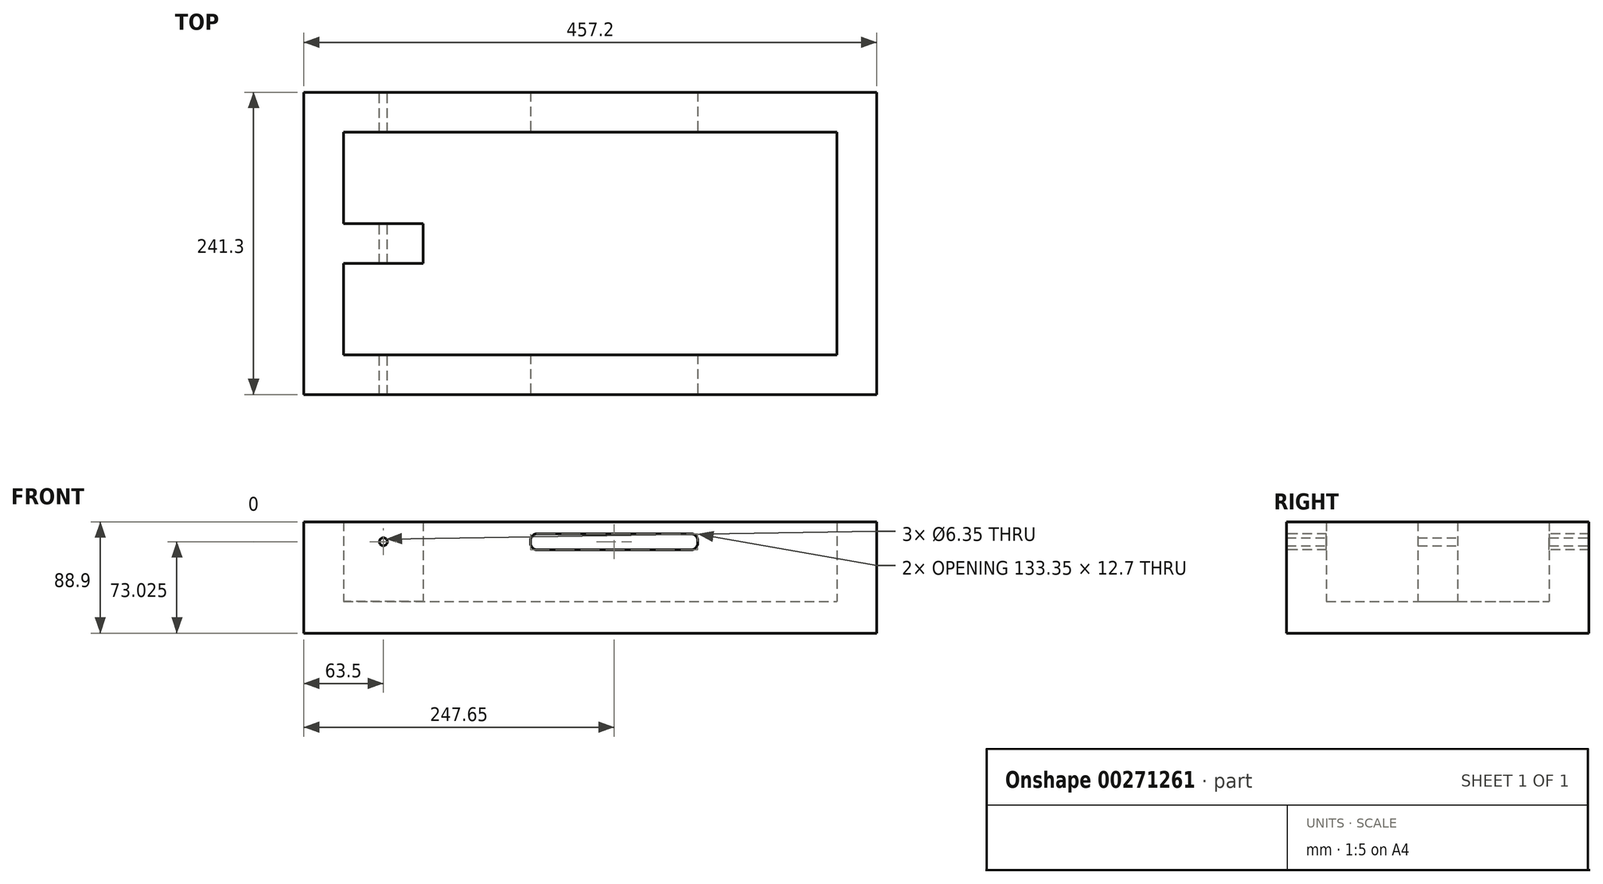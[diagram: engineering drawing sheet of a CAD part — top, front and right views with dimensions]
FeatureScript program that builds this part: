
annotation { "Feature Type Name" : "Feature", "Feature Type Description" : "" }
export const myFeature = defineFeature(function(context is Context, id is Id, definition is map)
    precondition{}
    {
        {
            var Q0;
            Q0=qCreatedBy(makeId("Front.planeOp"),FACE);
            var sketch = newSketch(context, id + "F0", { "sketchPlane" : qUnion([Q0])});
            skLineSegment(sketch, "E0.bottom", {"start": v(0, 0) * mm, "end": v(457.2, 0) * mm});
            skLineSegment(sketch, "E0.top", {"start": v(0, 63.5) * mm, "end": v(457.2, 63.5) * mm});
            skLineSegment(sketch, "E0.left", {"start": v(0, 0) * mm, "end": v(0, 63.5) * mm});
            skLineSegment(sketch, "E0.right", {"start": v(457.2, 0) * mm, "end": v(457.2, 63.5) * mm});
            skSolve(sketch);
        }
        {
            var Q0;
            Q0=makeQuery(id+"F0.imprint","IMPRINT",FACE,{"disambiguationData":[TD([[makeQuery(id+"F0.imprint","IMPRINT",EDGE,{"derivedFrom":sQuery(id+"F0.wireOp",EDGE,"E0.bottom")}),1.0]])]});
            extrude(context, id + "F1", {"entities" : qUnion([Q0]), "depth" : 31.75 * mm});
        }
        {
            var Q0;
            Q0=makeQuery(id+"F1.opExtrude","CAP_FACE",FACE,{"disambiguationData":[OSD([sQuery(id+"F0.wireOp",EDGE,"E0.bottom"),sQuery(id+"F0.wireOp",EDGE,"E0.top"),sQuery(id+"F0.wireOp",EDGE,"E0.left"),sQuery(id+"F0.wireOp",EDGE,"E0.right")])],"isStart":false});
            var sketch = newSketch(context, id + "F2", { "sketchPlane" : qUnion([Q0])});
            skLineSegment(sketch, "E1.bottom", {"start": v(457.2, 63.5) * mm, "end": v(425.45, 63.5) * mm});
            skLineSegment(sketch, "E1.top", {"start": v(457.2, 0) * mm, "end": v(425.45, 0) * mm});
            skLineSegment(sketch, "E1.left", {"start": v(457.2, 63.5) * mm, "end": v(457.2, 0) * mm});
            skLineSegment(sketch, "E1.right", {"start": v(425.45, 63.5) * mm, "end": v(425.45, 0) * mm});
            skSolve(sketch);
        }
        {
            var Q0;
            Q0=makeQuery(id+"F2.imprint","IMPRINT",FACE,{"disambiguationData":[TD([[makeQuery(id+"F2.imprint","IMPRINT",EDGE,{"derivedFrom":sQuery(id+"F2.wireOp",EDGE,"E1.bottom")}),-1.0]])]});
            extrude(context, id + "F3", {"entities" : qUnion([Q0]), "operationType" : NewBodyOperationType.ADD, "depth" : 177.8 * mm});
        }
        {
            var Q0;
            Q0=makeQuery(id+"F3.opExtrude","CAP_FACE",FACE,{"disambiguationData":[OSD([sQuery(id+"F2.wireOp",EDGE,"E1.bottom"),sQuery(id+"F2.wireOp",EDGE,"E1.top"),sQuery(id+"F2.wireOp",EDGE,"E1.left"),sQuery(id+"F2.wireOp",EDGE,"E1.right")])],"isStart":false});
            var sketch = newSketch(context, id + "F4", { "sketchPlane" : qUnion([Q0])});
            skLineSegment(sketch, "E2.bottom", {"start": v(457.2, 0) * mm, "end": v(0, 0) * mm});
            skLineSegment(sketch, "E2.top", {"start": v(457.2, 63.5) * mm, "end": v(0, 63.5) * mm});
            skLineSegment(sketch, "E2.left", {"start": v(457.2, 0) * mm, "end": v(457.2, 63.5) * mm});
            skLineSegment(sketch, "E2.right", {"start": v(0, 0) * mm, "end": v(0, 63.5) * mm});
            skSolve(sketch);
        }
        {
            var Q0;
            {var subQ0=sQuery(id+"F4.wireOp",EDGE,"E2.left");Q0=makeQuery(id+"F4.imprint","IMPRINT",FACE,{"disambiguationData":[TD([[makeQuery(id+"F4.imprint","IMPRINT",EDGE,{"derivedFrom":subQ0}),1.0]])]});}
            var Q1;
            {var subQ2=sQuery(id+"F4.wireOp",EDGE,"E2.right");Q1=makeQuery(id+"F4.imprint","IMPRINT",FACE,{"disambiguationData":[TD([[makeQuery(id+"F4.imprint","IMPRINT",EDGE,{"derivedFrom":subQ2}),-1.0]])]});}
            extrude(context, id + "F5", {"entities" : qUnion([Q0, Q1]), "operationType" : NewBodyOperationType.ADD, "depth" : 31.75 * mm});
        }
        {
            var Q0;
            Q0=makeQuery(id+"F1.opExtrude","CAP_FACE",FACE,{"disambiguationData":[OSD([sQuery(id+"F0.wireOp",EDGE,"E0.bottom"),sQuery(id+"F0.wireOp",EDGE,"E0.top"),sQuery(id+"F0.wireOp",EDGE,"E0.left"),sQuery(id+"F0.wireOp",EDGE,"E0.right")])],"isStart":false});
            var sketch = newSketch(context, id + "F6", { "sketchPlane" : qUnion([Q0])});
            skLineSegment(sketch, "E3.bottom", {"start": v(0, 63.5) * mm, "end": v(31.75, 63.5) * mm});
            skLineSegment(sketch, "E3.top", {"start": v(0, 0) * mm, "end": v(31.75, 0) * mm});
            skLineSegment(sketch, "E3.left", {"start": v(0, 63.5) * mm, "end": v(0, 0) * mm});
            skLineSegment(sketch, "E3.right", {"start": v(31.75, 63.5) * mm, "end": v(31.75, 0) * mm});
            skSolve(sketch);
        }
        {
            var Q0;
            Q0=makeQuery(id+"F6.imprint","IMPRINT",FACE,{"disambiguationData":[TD([[makeQuery(id+"F6.imprint","IMPRINT",EDGE,{"derivedFrom":sQuery(id+"F6.wireOp",EDGE,"E3.bottom")}),-1.0]])]});
            extrude(context, id + "F7", {"entities" : qUnion([Q0]), "operationType" : NewBodyOperationType.ADD, "depth" : 177.8 * mm});
        }
        {
            var Q0;
            Q0=makeQuery(id+"F7.opExtrude","SWEPT_FACE",FACE,{"disambiguationData":[OSD([sQuery(id+"F6.wireOp",EDGE,"E3.right")])]});
            var sketch = newSketch(context, id + "F8", { "sketchPlane" : qUnion([Q0])});
            skLineSegment(sketch, "E4", {"start": v(-209.55, 63.5) * mm, "end": v(-120.65, 63.5) * mm});
            skLineSegment(sketch, "E5", {"start": v(-120.65, 63.5) * mm, "end": v(-120.65, 0) * mm});
            skLineSegment(sketch, "E6.bottom", {"start": v(-136.53, 63.5) * mm, "end": v(-104.78, 63.5) * mm});
            skLineSegment(sketch, "E6.top", {"start": v(-136.53, 0) * mm, "end": v(-104.78, 0) * mm});
            skLineSegment(sketch, "E6.left", {"start": v(-136.53, 63.5) * mm, "end": v(-136.53, 0) * mm});
            skLineSegment(sketch, "E6.right", {"start": v(-104.78, 63.5) * mm, "end": v(-104.78, 0) * mm});
            skPoint(sketch, "E6.middle", {"position": v(-120.65, 31.75) * mm});
            skSolve(sketch);
        }
        {
            var Q0;
            {var subQ0=sQuery(id+"F8.wireOp",EDGE,"E5");Q0=makeQuery(id+"F8.imprint","IMPRINT",FACE,{"disambiguationData":[TD([[makeQuery(id+"F8.imprint","IMPRINT",EDGE,{"derivedFrom":subQ0}),-1.0]])]});}
            var Q1;
            {var subQ0=sQuery(id+"F8.wireOp",EDGE,"E5");Q1=makeQuery(id+"F8.imprint","IMPRINT",FACE,{"disambiguationData":[TD([[makeQuery(id+"F8.imprint","IMPRINT",EDGE,{"derivedFrom":subQ0}),1.0]])]});}
            extrude(context, id + "F9", {"entities" : qUnion([Q0, Q1]), "operationType" : NewBodyOperationType.ADD, "depth" : 63.5 * mm});
        }
        {
            var Q0;
            Q0=makeQuery(id+"F9.opExtrude","SWEPT_FACE",FACE,{"disambiguationData":[OSD([sQuery(id+"F8.wireOp",EDGE,"E6.left")])]});
            var sketch = newSketch(context, id + "F10", { "sketchPlane" : qUnion([Q0])});
            skCircle(sketch, "E7", {"center": v(63.5, 47.62) * mm, "radius": 3.18 * mm});
            skPoint(sketch, "E7.centerSnap0", {"position": v(31.75, 31.75) * mm});
            skPoint(sketch, "E7.centerSnap1", {"position": v(63.5, 63.5) * mm});
            skSolve(sketch);
        }
        {
            var Q0;
            Q0 = qSketchRegion(id + "F10", true);
            extrude(context, id + "F11", {"entities" : qUnion([Q0]), "operationType" : NewBodyOperationType.REMOVE, "endBound" : BoundingType.SYMMETRIC, "depth" : 381 * mm});
        }
        {
            var Q0;
            Q0=makeQuery(id+"F9.boolean.opBoolean","MERGE",FACE,{"derivedFrom":[makeQuery(id+"F7.boolean.opBoolean","MERGE",FACE,{"derivedFrom":[makeQuery(id+"F5.boolean.opBoolean","MERGE",FACE,{"derivedFrom":[makeQuery(id+"F3.boolean.opBoolean","MERGE",FACE,{"derivedFrom":[makeQuery(id+"F1.opExtrude","SWEPT_FACE",FACE,{"disambiguationData":[OSD([sQuery(id+"F0.wireOp",EDGE,"E0.bottom")])]}),makeQuery(id+"F3.opExtrude","SWEPT_FACE",FACE,{"disambiguationData":[OSD([sQuery(id+"F2.wireOp",EDGE,"E1.top")])]})]}),makeQuery(id+"F5.opExtrude","SWEPT_FACE",FACE,{"disambiguationData":[OSD([sQuery(id+"F4.wireOp",EDGE,"E2.bottom")])]})]}),makeQuery(id+"F7.opExtrude","SWEPT_FACE",FACE,{"disambiguationData":[OSD([sQuery(id+"F6.wireOp",EDGE,"E3.top")])]})]}),makeQuery(id+"F9.opExtrude","SWEPT_FACE",FACE,{"disambiguationData":[OSD([sQuery(id+"F8.wireOp",EDGE,"E6.top")])]})]});
            var sketch = newSketch(context, id + "F12", { "sketchPlane" : qUnion([Q0])});
            skLineSegment(sketch, "E8.bottom", {"start": v(0, 241.3) * mm, "end": v(457.2, 241.3) * mm});
            skLineSegment(sketch, "E8.top", {"start": v(0, 0) * mm, "end": v(457.2, 0) * mm});
            skLineSegment(sketch, "E8.left", {"start": v(0, 241.3) * mm, "end": v(0, 0) * mm});
            skLineSegment(sketch, "E8.right", {"start": v(457.2, 241.3) * mm, "end": v(457.2, 0) * mm});
            skSolve(sketch);
        }
        {
            var Q0;
            Q0=makeQuery(id+"F12.imprint","IMPRINT",FACE,{"disambiguationData":[TD([[makeQuery(id+"F12.imprint","IMPRINT",EDGE,{"derivedFrom":sQuery(id+"F12.wireOp",EDGE,"E8.bottom")}),-1.0]])]});
            var Q1;
            {var subQ4=sQuery(id+"F0.wireOp",EDGE,"E0.bottom");Q1=makeQuery(id+"F12.imprint","IMPRINT",FACE,{"disambiguationData":[TD([[makeQuery(id+"F12.imprint","IMPRINT",EDGE,{"derivedFrom":makeQuery(id+"F1.opExtrude","CAP_EDGE",EDGE,{"disambiguationData":[OSD([subQ4])],"isStart":false})}),1.0]])]});}
            extrude(context, id + "F13", {"entities" : qUnion([Q0, Q1]), "operationType" : NewBodyOperationType.ADD, "depth" : 25.4 * mm});
        }
        {
            var Q0;
            Q0=makeQuery(id+"F13.boolean.opBoolean","MERGE",FACE,{"derivedFrom":[makeQuery(id+"F5.opExtrude","CAP_FACE",FACE,{"disambiguationData":[OSD([sQuery(id+"F4.wireOp",EDGE,"E2.bottom"),sQuery(id+"F4.wireOp",EDGE,"E2.top"),sQuery(id+"F4.wireOp",EDGE,"E2.left"),sQuery(id+"F4.wireOp",EDGE,"E2.right")])],"isStart":false}),makeQuery(id+"F13.opExtrude","SWEPT_FACE",FACE,{"disambiguationData":[OSD([sQuery(id+"F12.wireOp",EDGE,"E8.bottom")])]})]});
            var sketch = newSketch(context, id + "F14", { "sketchPlane" : qUnion([Q0])});
            skLineSegment(sketch, "E9", {"start": v(457.2, 63.5) * mm, "end": v(393.7, 63.5) * mm});
            skLineSegment(sketch, "E10", {"start": v(393.7, 63.5) * mm, "end": v(101.6, 63.5) * mm});
            skLineSegment(sketch, "E11", {"start": v(101.6, 63.5) * mm, "end": v(247.65, 63.5) * mm});
            skLineSegment(sketch, "E12", {"start": v(247.65, 63.5) * mm, "end": v(247.65, 47.62) * mm});
            skLineSegment(sketch, "E13.bottom", {"start": v(314.33, 41.28) * mm, "end": v(180.98, 41.28) * mm});
            skLineSegment(sketch, "E13.top", {"start": v(314.33, 53.97) * mm, "end": v(180.98, 53.97) * mm});
            skLineSegment(sketch, "E13.left", {"start": v(314.33, 41.28) * mm, "end": v(314.33, 53.98) * mm});
            skLineSegment(sketch, "E13.right", {"start": v(180.98, 41.28) * mm, "end": v(180.98, 53.98) * mm});
            skPoint(sketch, "E13.middle", {"position": v(247.65, 47.62) * mm});
            skSolve(sketch);
        }
        {
            var Q0;
            Q0=makeQuery(id+"F14.imprint","IMPRINT",FACE,{"disambiguationData":[TD([[makeQuery(id+"F14.imprint","IMPRINT",EDGE,{"derivedFrom":sQuery(id+"F14.wireOp",EDGE,"E13.bottom")}),-1.0]])]});
            extrude(context, id + "F15", {"entities" : qUnion([Q0]), "operationType" : NewBodyOperationType.REMOVE, "oppositeDirection" : true, "depth" : 254 * mm});
        }
        {
            var Q0;
            {var subQ4=sQuery(id+"F14.wireOp",EDGE,"E13.bottom");var subQ5=sQuery(id+"F14.wireOp",EDGE,"E13.right");Q0=makeQuery(id+"F15.boolean.opBoolean","COPY",EDGE,{"disambiguationData":[TD([makeQuery(id+"F13.opExtrude","SWEPT_FACE",FACE,{"disambiguationData":[OSD([sQuery(id+"F12.wireOp",EDGE,"E8.bottom")])]})])],"derivedFrom":makeQuery(id+"F15.opExtrude","SWEPT_EDGE",EDGE,{"disambiguationData":[OSD([subQ4,subQ5])]})});}
            var Q1;
            {var subQ4=sQuery(id+"F14.wireOp",EDGE,"E13.top");var subQ5=sQuery(id+"F14.wireOp",EDGE,"E13.right");Q1=makeQuery(id+"F15.boolean.opBoolean","COPY",EDGE,{"disambiguationData":[TD([makeQuery(id+"F13.opExtrude","SWEPT_FACE",FACE,{"disambiguationData":[OSD([sQuery(id+"F12.wireOp",EDGE,"E8.bottom")])]})])],"derivedFrom":makeQuery(id+"F15.opExtrude","SWEPT_EDGE",EDGE,{"disambiguationData":[OSD([subQ4,subQ5])]})});}
            var Q2;
            {var subQ4=sQuery(id+"F14.wireOp",EDGE,"E13.bottom");var subQ5=sQuery(id+"F14.wireOp",EDGE,"E13.left");Q2=makeQuery(id+"F15.boolean.opBoolean","COPY",EDGE,{"disambiguationData":[TD([makeQuery(id+"F13.opExtrude","SWEPT_FACE",FACE,{"disambiguationData":[OSD([sQuery(id+"F12.wireOp",EDGE,"E8.bottom")])]})])],"derivedFrom":makeQuery(id+"F15.opExtrude","SWEPT_EDGE",EDGE,{"disambiguationData":[OSD([subQ4,subQ5])]})});}
            var Q3;
            {var subQ4=sQuery(id+"F14.wireOp",EDGE,"E13.top");var subQ5=sQuery(id+"F14.wireOp",EDGE,"E13.left");Q3=makeQuery(id+"F15.boolean.opBoolean","COPY",EDGE,{"disambiguationData":[TD([makeQuery(id+"F13.opExtrude","SWEPT_FACE",FACE,{"disambiguationData":[OSD([sQuery(id+"F12.wireOp",EDGE,"E8.bottom")])]})])],"derivedFrom":makeQuery(id+"F15.opExtrude","SWEPT_EDGE",EDGE,{"disambiguationData":[OSD([subQ4,subQ5])]})});}
            var Q4;
            {var subQ0=sQuery(id+"F14.wireOp",EDGE,"E13.bottom");var subQ5=sQuery(id+"F14.wireOp",EDGE,"E13.right");Q4=makeQuery(id+"F15.boolean.opBoolean","COPY",EDGE,{"disambiguationData":[TD([makeQuery(id+"F13.opExtrude","SWEPT_FACE",FACE,{"disambiguationData":[OSD([sQuery(id+"F12.wireOp",EDGE,"E8.top")])]})])],"derivedFrom":makeQuery(id+"F15.opExtrude","SWEPT_EDGE",EDGE,{"disambiguationData":[OSD([subQ0,subQ5])]})});}
            var Q5;
            {var subQ0=sQuery(id+"F14.wireOp",EDGE,"E13.top");var subQ5=sQuery(id+"F14.wireOp",EDGE,"E13.right");Q5=makeQuery(id+"F15.boolean.opBoolean","COPY",EDGE,{"disambiguationData":[TD([makeQuery(id+"F13.opExtrude","SWEPT_FACE",FACE,{"disambiguationData":[OSD([sQuery(id+"F12.wireOp",EDGE,"E8.top")])]})])],"derivedFrom":makeQuery(id+"F15.opExtrude","SWEPT_EDGE",EDGE,{"disambiguationData":[OSD([subQ0,subQ5])]})});}
            var Q6;
            {var subQ0=sQuery(id+"F14.wireOp",EDGE,"E13.bottom");var subQ5=sQuery(id+"F14.wireOp",EDGE,"E13.left");Q6=makeQuery(id+"F15.boolean.opBoolean","COPY",EDGE,{"disambiguationData":[TD([makeQuery(id+"F13.opExtrude","SWEPT_FACE",FACE,{"disambiguationData":[OSD([sQuery(id+"F12.wireOp",EDGE,"E8.top")])]})])],"derivedFrom":makeQuery(id+"F15.opExtrude","SWEPT_EDGE",EDGE,{"disambiguationData":[OSD([subQ0,subQ5])]})});}
            var Q7;
            {var subQ0=sQuery(id+"F14.wireOp",EDGE,"E13.top");var subQ5=sQuery(id+"F14.wireOp",EDGE,"E13.left");Q7=makeQuery(id+"F15.boolean.opBoolean","COPY",EDGE,{"disambiguationData":[TD([makeQuery(id+"F13.opExtrude","SWEPT_FACE",FACE,{"disambiguationData":[OSD([sQuery(id+"F12.wireOp",EDGE,"E8.top")])]})])],"derivedFrom":makeQuery(id+"F15.opExtrude","SWEPT_EDGE",EDGE,{"disambiguationData":[OSD([subQ0,subQ5])]})});}
            fillet(context, id + "F16", {"entities" : qUnion([Q0, Q1, Q2, Q3, Q4, Q5, Q6, Q7]), "radius" : 5.08 * mm, "tangentPropagation" : true, "allowEdgeOverflow" : false});
        }
    });
